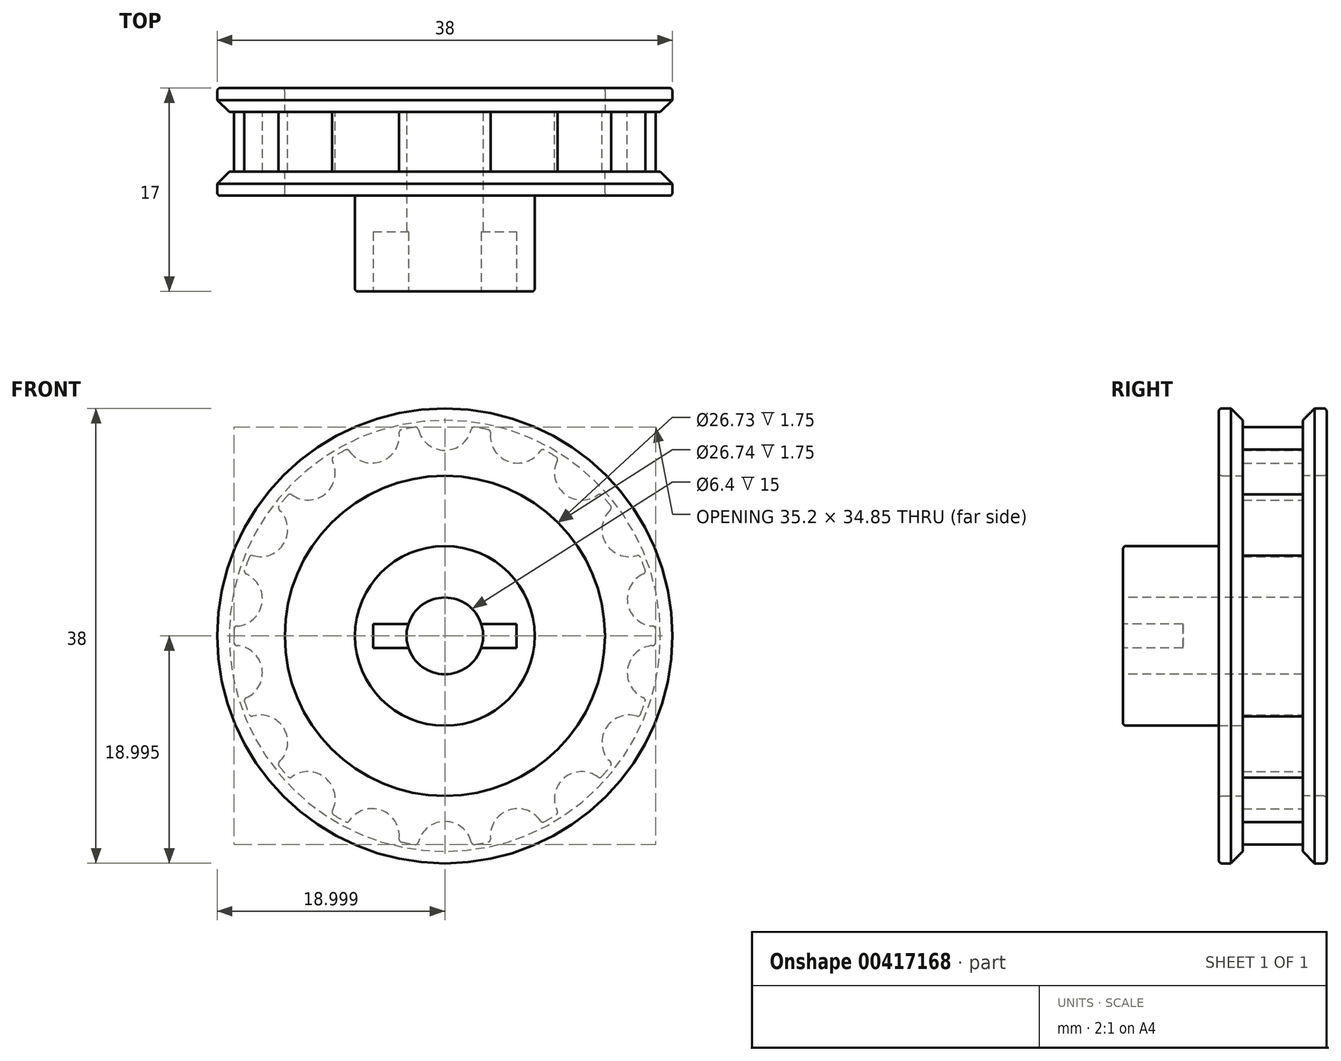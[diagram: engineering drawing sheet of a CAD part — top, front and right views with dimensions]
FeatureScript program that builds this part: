
annotation { "Feature Type Name" : "Feature", "Feature Type Description" : "" }
export const myFeature = defineFeature(function(context is Context, id is Id, definition is map)
    precondition{}
    {
        {
            var Q0;
            Q0=qCreatedBy(makeId("Front.planeOp"),FACE);
            var sketch = newSketch(context, id + "F0", { "sketchPlane" : qUnion([Q0])});
            skCircle(sketch, "E0", {"center": v(-33.37, 18.9) * mm, "radius": 20.2 * mm});
            skCircle(sketch, "E1", {"center": v(-33.37, 18.9) * mm, "radius": 17.78 * mm, "construction": true});
            skCircle(sketch, "E2", {"center": v(-33.37, 36.69) * mm, "radius": 2.28 * mm});
            skCircle(sketch, "E3.1.0", {"center": v(-39.45, 35.61) * mm, "radius": 2.28 * mm});
            skCircle(sketch, "E3.2.0", {"center": v(-44.8, 32.53) * mm, "radius": 2.28 * mm});
            skCircle(sketch, "E3.3.0", {"center": v(-48.77, 27.8) * mm, "radius": 2.28 * mm});
            skCircle(sketch, "E3.4.0", {"center": v(-50.88, 22) * mm, "radius": 2.28 * mm});
            skCircle(sketch, "E3.5.0", {"center": v(-50.88, 15.82) * mm, "radius": 2.28 * mm});
            skCircle(sketch, "E3.6.0", {"center": v(-48.77, 10.01) * mm, "radius": 2.28 * mm});
            skCircle(sketch, "E3.7.0", {"center": v(-44.8, 5.28) * mm, "radius": 2.28 * mm});
            skCircle(sketch, "E3.8.0", {"center": v(-39.45, 2.2) * mm, "radius": 2.28 * mm});
            skCircle(sketch, "E3.9.0", {"center": v(-33.37, 1.12) * mm, "radius": 2.28 * mm});
            skCircle(sketch, "E3.10.0", {"center": v(-27.29, 2.2) * mm, "radius": 2.28 * mm});
            skCircle(sketch, "E3.11.0", {"center": v(-21.94, 5.28) * mm, "radius": 2.28 * mm});
            skCircle(sketch, "E3.12.0", {"center": v(-17.97, 10.01) * mm, "radius": 2.28 * mm});
            skCircle(sketch, "E3.13.0", {"center": v(-15.86, 15.82) * mm, "radius": 2.28 * mm});
            skCircle(sketch, "E3.14.0", {"center": v(-15.86, 22) * mm, "radius": 2.28 * mm});
            skCircle(sketch, "E3.15.0", {"center": v(-17.97, 27.8) * mm, "radius": 2.28 * mm});
            skCircle(sketch, "E3.16.0", {"center": v(-21.94, 32.53) * mm, "radius": 2.28 * mm});
            skCircle(sketch, "E3.17.0", {"center": v(-27.29, 35.61) * mm, "radius": 2.28 * mm});
            skSolve(sketch);
        }
        {
            var Q0;
            Q0 = qSketchRegion(id + "F0", true);
            extrude(context, id + "F1", {"entities" : qUnion([Q0]), "depth" : 5 * mm, "offsetDistance" : 25 * mm});
        }
        {
            var Q0;
            Q0=makeQuery(id+"F1.opExtrude","CAP_FACE",FACE,{"disambiguationData":[OSD([sQuery(id+"F0.wireOp",EDGE,"E0"),sQuery(id+"F0.wireOp",EDGE,"E2"),sQuery(id+"F0.wireOp",EDGE,"E3.1.0"),sQuery(id+"F0.wireOp",EDGE,"E3.2.0"),sQuery(id+"F0.wireOp",EDGE,"E3.3.0"),sQuery(id+"F0.wireOp",EDGE,"E3.4.0"),sQuery(id+"F0.wireOp",EDGE,"E3.5.0"),sQuery(id+"F0.wireOp",EDGE,"E3.6.0"),sQuery(id+"F0.wireOp",EDGE,"E3.7.0"),sQuery(id+"F0.wireOp",EDGE,"E3.8.0"),sQuery(id+"F0.wireOp",EDGE,"E3.9.0"),sQuery(id+"F0.wireOp",EDGE,"E3.10.0"),sQuery(id+"F0.wireOp",EDGE,"E3.11.0"),sQuery(id+"F0.wireOp",EDGE,"E3.12.0"),sQuery(id+"F0.wireOp",EDGE,"E3.13.0"),sQuery(id+"F0.wireOp",EDGE,"E3.14.0"),sQuery(id+"F0.wireOp",EDGE,"E3.15.0"),sQuery(id+"F0.wireOp",EDGE,"E3.16.0"),sQuery(id+"F0.wireOp",EDGE,"E3.17.0"),sQuery(id+"F0.wireOp",EDGE,"E3.18.0"),sQuery(id+"F0.wireOp",EDGE,"E3.19.0")])],"isStart":false});
            var sketch = newSketch(context, id + "F2", { "sketchPlane" : qUnion([Q0])});
            skCircle(sketch, "E4", {"center": v(-33.37, 18.9) * mm, "radius": 17.6 * mm});
            skCircle(sketch, "E5", {"center": v(-33.37, 18.9) * mm, "radius": 21.36 * mm});
            skSolve(sketch);
        }
        {
            var Q0;
            Q0 = qSketchRegion(id + "F2", true);
            extrude(context, id + "F3", {"entities" : qUnion([Q0]), "operationType" : NewBodyOperationType.REMOVE, "oppositeDirection" : true, "depth" : 5 * mm, "offsetDistance" : 25 * mm});
        }
        {
            var Q0;
            Q0=makeQuery(id+"F1.opExtrude","CAP_FACE",FACE,{"disambiguationData":[OSD([sQuery(id+"F0.wireOp",EDGE,"E0"),sQuery(id+"F0.wireOp",EDGE,"E2"),sQuery(id+"F0.wireOp",EDGE,"E3.1.0"),sQuery(id+"F0.wireOp",EDGE,"E3.2.0"),sQuery(id+"F0.wireOp",EDGE,"E3.3.0"),sQuery(id+"F0.wireOp",EDGE,"E3.4.0"),sQuery(id+"F0.wireOp",EDGE,"E3.5.0"),sQuery(id+"F0.wireOp",EDGE,"E3.6.0"),sQuery(id+"F0.wireOp",EDGE,"E3.7.0"),sQuery(id+"F0.wireOp",EDGE,"E3.8.0"),sQuery(id+"F0.wireOp",EDGE,"E3.9.0"),sQuery(id+"F0.wireOp",EDGE,"E3.10.0"),sQuery(id+"F0.wireOp",EDGE,"E3.11.0"),sQuery(id+"F0.wireOp",EDGE,"E3.12.0"),sQuery(id+"F0.wireOp",EDGE,"E3.13.0"),sQuery(id+"F0.wireOp",EDGE,"E3.14.0"),sQuery(id+"F0.wireOp",EDGE,"E3.15.0"),sQuery(id+"F0.wireOp",EDGE,"E3.16.0"),sQuery(id+"F0.wireOp",EDGE,"E3.17.0"),sQuery(id+"F0.wireOp",EDGE,"E3.18.0"),sQuery(id+"F0.wireOp",EDGE,"E3.19.0")])],"isStart":false});
            var sketch = newSketch(context, id + "F4", { "sketchPlane" : qUnion([Q0])});
            skCircle(sketch, "E6", {"center": v(-33.37, 18.9) * mm, "radius": 13.37 * mm});
            skCircle(sketch, "E7", {"center": v(-33.37, 18.9) * mm, "radius": 19 * mm});
            skSolve(sketch);
        }
        {
            var Q0;
            Q0=makeQuery(id+"F4.imprint","IMPRINT",FACE,{"disambiguationData":[TD([[makeQuery(id+"F4.imprint","IMPRINT",EDGE,{"derivedFrom":sQuery(id+"F4.wireOp",EDGE,"E7")}),1.0]])]});
            var Q1;
            Q1=makeQuery(id+"F4.imprint","IMPRINT",FACE,{"disambiguationData":[TD([[makeQuery(id+"F4.imprint","IMPRINT",EDGE,{"derivedFrom":sQuery(id+"F4.wireOp",EDGE,"E6")}),-1.0]])]});
            extrude(context, id + "F5", {"entities" : qUnion([Q0, Q1]), "operationType" : NewBodyOperationType.ADD, "depth" : 2 * mm, "offsetDistance" : 25 * mm});
        }
        {
            var Q0;
            Q0=makeQuery(id+"F5.opExtrude","CAP_EDGE",EDGE,{"disambiguationData":[OSD([sQuery(id+"F4.wireOp",EDGE,"E7")])],"isStart":true});
            chamfer(context, id + "F6", {"entities" : qUnion([Q0]), "chamferType" : ChamferType.OFFSET_ANGLE, "width" : 1 * mm, "oppositeDirection" : false, "angle" : 45 * degree, "tangentPropagation" : true});
        }
        {
            var Q0;
            Q0=makeQuery(id+"F1.opExtrude","CAP_FACE",FACE,{"disambiguationData":[OSD([sQuery(id+"F0.wireOp",EDGE,"E0"),sQuery(id+"F0.wireOp",EDGE,"E2"),sQuery(id+"F0.wireOp",EDGE,"E3.1.0"),sQuery(id+"F0.wireOp",EDGE,"E3.2.0"),sQuery(id+"F0.wireOp",EDGE,"E3.3.0"),sQuery(id+"F0.wireOp",EDGE,"E3.4.0"),sQuery(id+"F0.wireOp",EDGE,"E3.5.0"),sQuery(id+"F0.wireOp",EDGE,"E3.6.0"),sQuery(id+"F0.wireOp",EDGE,"E3.7.0"),sQuery(id+"F0.wireOp",EDGE,"E3.8.0"),sQuery(id+"F0.wireOp",EDGE,"E3.9.0"),sQuery(id+"F0.wireOp",EDGE,"E3.10.0"),sQuery(id+"F0.wireOp",EDGE,"E3.11.0"),sQuery(id+"F0.wireOp",EDGE,"E3.12.0"),sQuery(id+"F0.wireOp",EDGE,"E3.13.0"),sQuery(id+"F0.wireOp",EDGE,"E3.14.0"),sQuery(id+"F0.wireOp",EDGE,"E3.15.0"),sQuery(id+"F0.wireOp",EDGE,"E3.16.0"),sQuery(id+"F0.wireOp",EDGE,"E3.17.0"),sQuery(id+"F0.wireOp",EDGE,"E3.18.0"),sQuery(id+"F0.wireOp",EDGE,"E3.19.0")])],"isStart":true});
            var sketch = newSketch(context, id + "F7", { "sketchPlane" : qUnion([Q0])});
            skCircle(sketch, "E8", {"center": v(33.37, 18.9) * mm, "radius": 13.37 * mm});
            skCircle(sketch, "E9", {"center": v(33.37, 18.9) * mm, "radius": 19 * mm});
            skSolve(sketch);
        }
        {
            var Q0;
            Q0=makeQuery(id+"F7.imprint","IMPRINT",FACE,{"disambiguationData":[TD([[makeQuery(id+"F7.imprint","IMPRINT",EDGE,{"derivedFrom":sQuery(id+"F7.wireOp",EDGE,"E8")}),-1.0]])]});
            var Q1;
            Q1=makeQuery(id+"F7.imprint","IMPRINT",FACE,{"disambiguationData":[TD([[makeQuery(id+"F7.imprint","IMPRINT",EDGE,{"derivedFrom":sQuery(id+"F7.wireOp",EDGE,"E9")}),1.0]])]});
            extrude(context, id + "F8", {"entities" : qUnion([Q0, Q1]), "operationType" : NewBodyOperationType.ADD, "depth" : 2 * mm, "offsetDistance" : 25 * mm});
        }
        {
            var Q0;
            Q0=makeQuery(id+"F8.opExtrude","CAP_EDGE",EDGE,{"disambiguationData":[OSD([sQuery(id+"F7.wireOp",EDGE,"E9")])],"isStart":true});
            chamfer(context, id + "F9", {"entities" : qUnion([Q0]), "chamferType" : ChamferType.OFFSET_ANGLE, "width" : 1 * mm, "oppositeDirection" : false, "angle" : 45 * degree, "tangentPropagation" : true});
        }
        {
            var Q0;
            Q0=makeQuery(id+"F1.opExtrude","CAP_FACE",FACE,{"disambiguationData":[OSD([sQuery(id+"F0.wireOp",EDGE,"E0"),sQuery(id+"F0.wireOp",EDGE,"E2"),sQuery(id+"F0.wireOp",EDGE,"E3.1.0"),sQuery(id+"F0.wireOp",EDGE,"E3.2.0"),sQuery(id+"F0.wireOp",EDGE,"E3.3.0"),sQuery(id+"F0.wireOp",EDGE,"E3.4.0"),sQuery(id+"F0.wireOp",EDGE,"E3.5.0"),sQuery(id+"F0.wireOp",EDGE,"E3.6.0"),sQuery(id+"F0.wireOp",EDGE,"E3.7.0"),sQuery(id+"F0.wireOp",EDGE,"E3.8.0"),sQuery(id+"F0.wireOp",EDGE,"E3.9.0"),sQuery(id+"F0.wireOp",EDGE,"E3.10.0"),sQuery(id+"F0.wireOp",EDGE,"E3.11.0"),sQuery(id+"F0.wireOp",EDGE,"E3.12.0"),sQuery(id+"F0.wireOp",EDGE,"E3.13.0"),sQuery(id+"F0.wireOp",EDGE,"E3.14.0"),sQuery(id+"F0.wireOp",EDGE,"E3.15.0"),sQuery(id+"F0.wireOp",EDGE,"E3.16.0"),sQuery(id+"F0.wireOp",EDGE,"E3.17.0"),sQuery(id+"F0.wireOp",EDGE,"E3.18.0"),sQuery(id+"F0.wireOp",EDGE,"E3.19.0")])],"isStart":false});
            var sketch = newSketch(context, id + "F10", { "sketchPlane" : qUnion([Q0])});
            skCircle(sketch, "E10", {"center": v(-33.37, 18.9) * mm, "radius": 7.5 * mm});
            skSolve(sketch);
        }
        {
            var Q0;
            Q0=makeQuery(id+"F10.imprint","IMPRINT",FACE,{"disambiguationData":[TD([[makeQuery(id+"F10.imprint","IMPRINT",EDGE,{"derivedFrom":sQuery(id+"F10.wireOp",EDGE,"E10")}),1.0]])]});
            extrude(context, id + "F11", {"entities" : qUnion([Q0]), "operationType" : NewBodyOperationType.ADD, "depth" : 10 * mm, "offsetDistance" : 25 * mm});
        }
        {
            var Q0;
            Q0=makeQuery(id+"F11.opExtrude","CAP_FACE",FACE,{"disambiguationData":[OSD([sQuery(id+"F10.wireOp",EDGE,"E10")])],"isStart":false});
            var sketch = newSketch(context, id + "F12", { "sketchPlane" : qUnion([Q0])});
            skCircle(sketch, "E11", {"center": v(-33.37, 18.9) * mm, "radius": 3.2 * mm});
            skSolve(sketch);
        }
        {
            var Q0;
            Q0=makeQuery(id+"F12.imprint","IMPRINT",FACE,{"disambiguationData":[TD([[makeQuery(id+"F12.imprint","IMPRINT",EDGE,{"derivedFrom":sQuery(id+"F12.wireOp",EDGE,"E11")}),1.0]])]});
            extrude(context, id + "F13", {"entities" : qUnion([Q0]), "operationType" : NewBodyOperationType.REMOVE, "oppositeDirection" : true, "depth" : 15 * mm, "offsetDistance" : 25 * mm});
        }
        {
            var Q0;
            Q0=makeQuery(id+"F11.opExtrude","CAP_FACE",FACE,{"disambiguationData":[OSD([sQuery(id+"F10.wireOp",EDGE,"E10")])],"isStart":false});
            var sketch = newSketch(context, id + "F14", { "sketchPlane" : qUnion([Q0])});
            skLineSegment(sketch, "E12.bottom", {"start": v(-39.37, 19.9) * mm, "end": v(-27.37, 19.9) * mm});
            skLineSegment(sketch, "E12.top", {"start": v(-39.37, 17.9) * mm, "end": v(-27.37, 17.9) * mm});
            skLineSegment(sketch, "E12.left", {"start": v(-39.37, 19.9) * mm, "end": v(-39.37, 17.9) * mm});
            skLineSegment(sketch, "E12.right", {"start": v(-27.37, 19.9) * mm, "end": v(-27.37, 17.9) * mm});
            skPoint(sketch, "E12.middle", {"position": v(-33.37, 18.9) * mm});
            skSolve(sketch);
        }
        {
            var Q0;
            {var subQ0=sQuery(id+"F14.wireOp",EDGE,"E12.left");Q0=makeQuery(id+"F14.imprint","IMPRINT",FACE,{"disambiguationData":[TD([[makeQuery(id+"F14.imprint","IMPRINT",EDGE,{"derivedFrom":subQ0}),1.0]])]});}
            var Q1;
            {var subQ0=sQuery(id+"F14.wireOp",EDGE,"E12.right");Q1=makeQuery(id+"F14.imprint","IMPRINT",FACE,{"disambiguationData":[TD([[makeQuery(id+"F14.imprint","IMPRINT",EDGE,{"derivedFrom":subQ0}),-1.0]])]});}
            extrude(context, id + "F15", {"entities" : qUnion([Q0, Q1]), "operationType" : NewBodyOperationType.REMOVE, "oppositeDirection" : true, "depth" : 5 * mm, "offsetDistance" : 25 * mm});
        }
        {
            var Q0;
            Q0=makeQuery(id+"F3.boolean.opBoolean","INTERSECT",EDGE,{"disambiguationData":[OD(1.0)],"derivedFrom":[makeQuery(id+"F1.opExtrude","SWEPT_FACE",FACE,{"disambiguationData":[OSD([sQuery(id+"F0.wireOp",EDGE,"E3.11.0")])]}),makeQuery(id+"F3.opExtrude","SWEPT_FACE",FACE,{"disambiguationData":[OSD([sQuery(id+"F2.wireOp",EDGE,"E4")])]})]});
            var Q1;
            Q1=makeQuery(id+"F3.boolean.opBoolean","INTERSECT",EDGE,{"disambiguationData":[OD(0.0)],"derivedFrom":[makeQuery(id+"F1.opExtrude","SWEPT_FACE",FACE,{"disambiguationData":[OSD([sQuery(id+"F0.wireOp",EDGE,"E3.11.0")])]}),makeQuery(id+"F3.opExtrude","SWEPT_FACE",FACE,{"disambiguationData":[OSD([sQuery(id+"F2.wireOp",EDGE,"E4")])]})]});
            var Q2;
            Q2=makeQuery(id+"F3.boolean.opBoolean","INTERSECT",EDGE,{"disambiguationData":[OD(1.0)],"derivedFrom":[makeQuery(id+"F1.opExtrude","SWEPT_FACE",FACE,{"disambiguationData":[OSD([sQuery(id+"F0.wireOp",EDGE,"E3.10.0")])]}),makeQuery(id+"F3.opExtrude","SWEPT_FACE",FACE,{"disambiguationData":[OSD([sQuery(id+"F2.wireOp",EDGE,"E4")])]})]});
            var Q3;
            Q3=makeQuery(id+"F3.boolean.opBoolean","INTERSECT",EDGE,{"disambiguationData":[OD(0.0)],"derivedFrom":[makeQuery(id+"F1.opExtrude","SWEPT_FACE",FACE,{"disambiguationData":[OSD([sQuery(id+"F0.wireOp",EDGE,"E3.12.0")])]}),makeQuery(id+"F3.opExtrude","SWEPT_FACE",FACE,{"disambiguationData":[OSD([sQuery(id+"F2.wireOp",EDGE,"E4")])]})]});
            var Q4;
            Q4=makeQuery(id+"F3.boolean.opBoolean","INTERSECT",EDGE,{"disambiguationData":[OD(1.0)],"derivedFrom":[makeQuery(id+"F1.opExtrude","SWEPT_FACE",FACE,{"disambiguationData":[OSD([sQuery(id+"F0.wireOp",EDGE,"E3.12.0")])]}),makeQuery(id+"F3.opExtrude","SWEPT_FACE",FACE,{"disambiguationData":[OSD([sQuery(id+"F2.wireOp",EDGE,"E4")])]})]});
            var Q5;
            Q5=makeQuery(id+"F3.boolean.opBoolean","INTERSECT",EDGE,{"disambiguationData":[OD(0.0)],"derivedFrom":[makeQuery(id+"F1.opExtrude","SWEPT_FACE",FACE,{"disambiguationData":[OSD([sQuery(id+"F0.wireOp",EDGE,"E3.13.0")])]}),makeQuery(id+"F3.opExtrude","SWEPT_FACE",FACE,{"disambiguationData":[OSD([sQuery(id+"F2.wireOp",EDGE,"E4")])]})]});
            var Q6;
            Q6=makeQuery(id+"F3.boolean.opBoolean","INTERSECT",EDGE,{"disambiguationData":[OD(1.0)],"derivedFrom":[makeQuery(id+"F1.opExtrude","SWEPT_FACE",FACE,{"disambiguationData":[OSD([sQuery(id+"F0.wireOp",EDGE,"E3.13.0")])]}),makeQuery(id+"F3.opExtrude","SWEPT_FACE",FACE,{"disambiguationData":[OSD([sQuery(id+"F2.wireOp",EDGE,"E4")])]})]});
            var Q7;
            Q7=makeQuery(id+"F3.boolean.opBoolean","INTERSECT",EDGE,{"disambiguationData":[OD(0.0)],"derivedFrom":[makeQuery(id+"F1.opExtrude","SWEPT_FACE",FACE,{"disambiguationData":[OSD([sQuery(id+"F0.wireOp",EDGE,"E3.14.0")])]}),makeQuery(id+"F3.opExtrude","SWEPT_FACE",FACE,{"disambiguationData":[OSD([sQuery(id+"F2.wireOp",EDGE,"E4")])]})]});
            var Q8;
            Q8=makeQuery(id+"F3.boolean.opBoolean","INTERSECT",EDGE,{"disambiguationData":[OD(1.0)],"derivedFrom":[makeQuery(id+"F1.opExtrude","SWEPT_FACE",FACE,{"disambiguationData":[OSD([sQuery(id+"F0.wireOp",EDGE,"E3.14.0")])]}),makeQuery(id+"F3.opExtrude","SWEPT_FACE",FACE,{"disambiguationData":[OSD([sQuery(id+"F2.wireOp",EDGE,"E4")])]})]});
            var Q9;
            Q9=makeQuery(id+"F3.boolean.opBoolean","INTERSECT",EDGE,{"disambiguationData":[OD(0.0)],"derivedFrom":[makeQuery(id+"F1.opExtrude","SWEPT_FACE",FACE,{"disambiguationData":[OSD([sQuery(id+"F0.wireOp",EDGE,"E3.15.0")])]}),makeQuery(id+"F3.opExtrude","SWEPT_FACE",FACE,{"disambiguationData":[OSD([sQuery(id+"F2.wireOp",EDGE,"E4")])]})]});
            fillet(context, id + "F16", {"entities" : qUnion([Q0, Q1, Q2, Q3, Q4, Q5, Q6, Q7, Q8, Q9]), "radius" : .25 * mm, "tangentPropagation" : true, "allowEdgeOverflow" : false});
        }
        {
            var Q0;
            Q0=makeQuery(id+"F3.boolean.opBoolean","INTERSECT",EDGE,{"disambiguationData":[OD(1.0)],"derivedFrom":[makeQuery(id+"F1.opExtrude","SWEPT_FACE",FACE,{"disambiguationData":[OSD([sQuery(id+"F0.wireOp",EDGE,"E3.15.0")])]}),makeQuery(id+"F3.opExtrude","SWEPT_FACE",FACE,{"disambiguationData":[OSD([sQuery(id+"F2.wireOp",EDGE,"E4")])]})]});
            var Q1;
            Q1=makeQuery(id+"F3.boolean.opBoolean","INTERSECT",EDGE,{"disambiguationData":[OD(0.0)],"derivedFrom":[makeQuery(id+"F1.opExtrude","SWEPT_FACE",FACE,{"disambiguationData":[OSD([sQuery(id+"F0.wireOp",EDGE,"E3.16.0")])]}),makeQuery(id+"F3.opExtrude","SWEPT_FACE",FACE,{"disambiguationData":[OSD([sQuery(id+"F2.wireOp",EDGE,"E4")])]})]});
            var Q2;
            Q2=makeQuery(id+"F3.boolean.opBoolean","INTERSECT",EDGE,{"disambiguationData":[OD(1.0)],"derivedFrom":[makeQuery(id+"F1.opExtrude","SWEPT_FACE",FACE,{"disambiguationData":[OSD([sQuery(id+"F0.wireOp",EDGE,"E3.16.0")])]}),makeQuery(id+"F3.opExtrude","SWEPT_FACE",FACE,{"disambiguationData":[OSD([sQuery(id+"F2.wireOp",EDGE,"E4")])]})]});
            var Q3;
            Q3=makeQuery(id+"F3.boolean.opBoolean","INTERSECT",EDGE,{"disambiguationData":[OD(1.0)],"derivedFrom":[makeQuery(id+"F1.opExtrude","SWEPT_FACE",FACE,{"disambiguationData":[OSD([sQuery(id+"F0.wireOp",EDGE,"E3.17.0")])]}),makeQuery(id+"F3.opExtrude","SWEPT_FACE",FACE,{"disambiguationData":[OSD([sQuery(id+"F2.wireOp",EDGE,"E4")])]})]});
            var Q4;
            Q4=makeQuery(id+"F3.boolean.opBoolean","INTERSECT",EDGE,{"disambiguationData":[OD(0.0)],"derivedFrom":[makeQuery(id+"F1.opExtrude","SWEPT_FACE",FACE,{"disambiguationData":[OSD([sQuery(id+"F0.wireOp",EDGE,"E3.17.0")])]}),makeQuery(id+"F3.opExtrude","SWEPT_FACE",FACE,{"disambiguationData":[OSD([sQuery(id+"F2.wireOp",EDGE,"E4")])]})]});
            var Q5;
            Q5=makeQuery(id+"F3.boolean.opBoolean","INTERSECT",EDGE,{"disambiguationData":[OD(1.0)],"derivedFrom":[makeQuery(id+"F1.opExtrude","SWEPT_FACE",FACE,{"disambiguationData":[OSD([sQuery(id+"F0.wireOp",EDGE,"E2")])]}),makeQuery(id+"F3.opExtrude","SWEPT_FACE",FACE,{"disambiguationData":[OSD([sQuery(id+"F2.wireOp",EDGE,"E4")])]})]});
            var Q6;
            Q6=makeQuery(id+"F3.boolean.opBoolean","INTERSECT",EDGE,{"disambiguationData":[OD(0.0)],"derivedFrom":[makeQuery(id+"F1.opExtrude","SWEPT_FACE",FACE,{"disambiguationData":[OSD([sQuery(id+"F0.wireOp",EDGE,"E2")])]}),makeQuery(id+"F3.opExtrude","SWEPT_FACE",FACE,{"disambiguationData":[OSD([sQuery(id+"F2.wireOp",EDGE,"E4")])]})]});
            var Q7;
            Q7=makeQuery(id+"F3.boolean.opBoolean","INTERSECT",EDGE,{"disambiguationData":[OD(0.0)],"derivedFrom":[makeQuery(id+"F1.opExtrude","SWEPT_FACE",FACE,{"disambiguationData":[OSD([sQuery(id+"F0.wireOp",EDGE,"E3.1.0")])]}),makeQuery(id+"F3.opExtrude","SWEPT_FACE",FACE,{"disambiguationData":[OSD([sQuery(id+"F2.wireOp",EDGE,"E4")])]})]});
            var Q8;
            Q8=makeQuery(id+"F3.boolean.opBoolean","INTERSECT",EDGE,{"disambiguationData":[OD(1.0)],"derivedFrom":[makeQuery(id+"F1.opExtrude","SWEPT_FACE",FACE,{"disambiguationData":[OSD([sQuery(id+"F0.wireOp",EDGE,"E3.1.0")])]}),makeQuery(id+"F3.opExtrude","SWEPT_FACE",FACE,{"disambiguationData":[OSD([sQuery(id+"F2.wireOp",EDGE,"E4")])]})]});
            var Q9;
            Q9=makeQuery(id+"F3.boolean.opBoolean","INTERSECT",EDGE,{"disambiguationData":[OD(0.0)],"derivedFrom":[makeQuery(id+"F1.opExtrude","SWEPT_FACE",FACE,{"disambiguationData":[OSD([sQuery(id+"F0.wireOp",EDGE,"E3.2.0")])]}),makeQuery(id+"F3.opExtrude","SWEPT_FACE",FACE,{"disambiguationData":[OSD([sQuery(id+"F2.wireOp",EDGE,"E4")])]})]});
            var Q10;
            Q10=makeQuery(id+"F3.boolean.opBoolean","INTERSECT",EDGE,{"disambiguationData":[OD(1.0)],"derivedFrom":[makeQuery(id+"F1.opExtrude","SWEPT_FACE",FACE,{"disambiguationData":[OSD([sQuery(id+"F0.wireOp",EDGE,"E3.2.0")])]}),makeQuery(id+"F3.opExtrude","SWEPT_FACE",FACE,{"disambiguationData":[OSD([sQuery(id+"F2.wireOp",EDGE,"E4")])]})]});
            var Q11;
            Q11=makeQuery(id+"F3.boolean.opBoolean","INTERSECT",EDGE,{"disambiguationData":[OD(0.0)],"derivedFrom":[makeQuery(id+"F1.opExtrude","SWEPT_FACE",FACE,{"disambiguationData":[OSD([sQuery(id+"F0.wireOp",EDGE,"E3.3.0")])]}),makeQuery(id+"F3.opExtrude","SWEPT_FACE",FACE,{"disambiguationData":[OSD([sQuery(id+"F2.wireOp",EDGE,"E4")])]})]});
            var Q12;
            Q12=makeQuery(id+"F3.boolean.opBoolean","INTERSECT",EDGE,{"disambiguationData":[OD(1.0)],"derivedFrom":[makeQuery(id+"F1.opExtrude","SWEPT_FACE",FACE,{"disambiguationData":[OSD([sQuery(id+"F0.wireOp",EDGE,"E3.3.0")])]}),makeQuery(id+"F3.opExtrude","SWEPT_FACE",FACE,{"disambiguationData":[OSD([sQuery(id+"F2.wireOp",EDGE,"E4")])]})]});
            var Q13;
            Q13=makeQuery(id+"F3.boolean.opBoolean","INTERSECT",EDGE,{"disambiguationData":[OD(0.0)],"derivedFrom":[makeQuery(id+"F1.opExtrude","SWEPT_FACE",FACE,{"disambiguationData":[OSD([sQuery(id+"F0.wireOp",EDGE,"E3.4.0")])]}),makeQuery(id+"F3.opExtrude","SWEPT_FACE",FACE,{"disambiguationData":[OSD([sQuery(id+"F2.wireOp",EDGE,"E4")])]})]});
            var Q14;
            Q14=makeQuery(id+"F3.boolean.opBoolean","INTERSECT",EDGE,{"disambiguationData":[OD(1.0)],"derivedFrom":[makeQuery(id+"F1.opExtrude","SWEPT_FACE",FACE,{"disambiguationData":[OSD([sQuery(id+"F0.wireOp",EDGE,"E3.4.0")])]}),makeQuery(id+"F3.opExtrude","SWEPT_FACE",FACE,{"disambiguationData":[OSD([sQuery(id+"F2.wireOp",EDGE,"E4")])]})]});
            var Q15;
            Q15=makeQuery(id+"F3.boolean.opBoolean","INTERSECT",EDGE,{"disambiguationData":[OD(0.0)],"derivedFrom":[makeQuery(id+"F1.opExtrude","SWEPT_FACE",FACE,{"disambiguationData":[OSD([sQuery(id+"F0.wireOp",EDGE,"E3.5.0")])]}),makeQuery(id+"F3.opExtrude","SWEPT_FACE",FACE,{"disambiguationData":[OSD([sQuery(id+"F2.wireOp",EDGE,"E4")])]})]});
            var Q16;
            Q16=makeQuery(id+"F3.boolean.opBoolean","INTERSECT",EDGE,{"disambiguationData":[OD(1.0)],"derivedFrom":[makeQuery(id+"F1.opExtrude","SWEPT_FACE",FACE,{"disambiguationData":[OSD([sQuery(id+"F0.wireOp",EDGE,"E3.5.0")])]}),makeQuery(id+"F3.opExtrude","SWEPT_FACE",FACE,{"disambiguationData":[OSD([sQuery(id+"F2.wireOp",EDGE,"E4")])]})]});
            var Q17;
            Q17=makeQuery(id+"F3.boolean.opBoolean","INTERSECT",EDGE,{"disambiguationData":[OD(1.0)],"derivedFrom":[makeQuery(id+"F1.opExtrude","SWEPT_FACE",FACE,{"disambiguationData":[OSD([sQuery(id+"F0.wireOp",EDGE,"E3.6.0")])]}),makeQuery(id+"F3.opExtrude","SWEPT_FACE",FACE,{"disambiguationData":[OSD([sQuery(id+"F2.wireOp",EDGE,"E4")])]})]});
            var Q18;
            Q18=makeQuery(id+"F3.boolean.opBoolean","INTERSECT",EDGE,{"disambiguationData":[OD(0.0)],"derivedFrom":[makeQuery(id+"F1.opExtrude","SWEPT_FACE",FACE,{"disambiguationData":[OSD([sQuery(id+"F0.wireOp",EDGE,"E3.6.0")])]}),makeQuery(id+"F3.opExtrude","SWEPT_FACE",FACE,{"disambiguationData":[OSD([sQuery(id+"F2.wireOp",EDGE,"E4")])]})]});
            var Q19;
            Q19=makeQuery(id+"F3.boolean.opBoolean","INTERSECT",EDGE,{"disambiguationData":[OD(0.0)],"derivedFrom":[makeQuery(id+"F1.opExtrude","SWEPT_FACE",FACE,{"disambiguationData":[OSD([sQuery(id+"F0.wireOp",EDGE,"E3.7.0")])]}),makeQuery(id+"F3.opExtrude","SWEPT_FACE",FACE,{"disambiguationData":[OSD([sQuery(id+"F2.wireOp",EDGE,"E4")])]})]});
            fillet(context, id + "F17", {"entities" : qUnion([Q0, Q1, Q2, Q3, Q4, Q5, Q6, Q7, Q8, Q9, Q10, Q11, Q12, Q13, Q14, Q15, Q16, Q17, Q18, Q19]), "radius" : .25 * mm, "tangentPropagation" : true, "allowEdgeOverflow" : false});
        }
        {
            var Q0;
            Q0=makeQuery(id+"F3.boolean.opBoolean","INTERSECT",EDGE,{"disambiguationData":[OD(1.0)],"derivedFrom":[makeQuery(id+"F1.opExtrude","SWEPT_FACE",FACE,{"disambiguationData":[OSD([sQuery(id+"F0.wireOp",EDGE,"E3.7.0")])]}),makeQuery(id+"F3.opExtrude","SWEPT_FACE",FACE,{"disambiguationData":[OSD([sQuery(id+"F2.wireOp",EDGE,"E4")])]})]});
            var Q1;
            Q1=makeQuery(id+"F3.boolean.opBoolean","INTERSECT",EDGE,{"disambiguationData":[OD(0.0)],"derivedFrom":[makeQuery(id+"F1.opExtrude","SWEPT_FACE",FACE,{"disambiguationData":[OSD([sQuery(id+"F0.wireOp",EDGE,"E3.8.0")])]}),makeQuery(id+"F3.opExtrude","SWEPT_FACE",FACE,{"disambiguationData":[OSD([sQuery(id+"F2.wireOp",EDGE,"E4")])]})]});
            var Q2;
            Q2=makeQuery(id+"F3.boolean.opBoolean","INTERSECT",EDGE,{"disambiguationData":[OD(1.0)],"derivedFrom":[makeQuery(id+"F1.opExtrude","SWEPT_FACE",FACE,{"disambiguationData":[OSD([sQuery(id+"F0.wireOp",EDGE,"E3.8.0")])]}),makeQuery(id+"F3.opExtrude","SWEPT_FACE",FACE,{"disambiguationData":[OSD([sQuery(id+"F2.wireOp",EDGE,"E4")])]})]});
            var Q3;
            Q3=makeQuery(id+"F3.boolean.opBoolean","INTERSECT",EDGE,{"disambiguationData":[OD(0.0)],"derivedFrom":[makeQuery(id+"F1.opExtrude","SWEPT_FACE",FACE,{"disambiguationData":[OSD([sQuery(id+"F0.wireOp",EDGE,"E3.9.0")])]}),makeQuery(id+"F3.opExtrude","SWEPT_FACE",FACE,{"disambiguationData":[OSD([sQuery(id+"F2.wireOp",EDGE,"E4")])]})]});
            var Q4;
            Q4=makeQuery(id+"F3.boolean.opBoolean","INTERSECT",EDGE,{"disambiguationData":[OD(1.0)],"derivedFrom":[makeQuery(id+"F1.opExtrude","SWEPT_FACE",FACE,{"disambiguationData":[OSD([sQuery(id+"F0.wireOp",EDGE,"E3.9.0")])]}),makeQuery(id+"F3.opExtrude","SWEPT_FACE",FACE,{"disambiguationData":[OSD([sQuery(id+"F2.wireOp",EDGE,"E4")])]})]});
            var Q5;
            Q5=makeQuery(id+"F3.boolean.opBoolean","INTERSECT",EDGE,{"disambiguationData":[OD(0.0)],"derivedFrom":[makeQuery(id+"F1.opExtrude","SWEPT_FACE",FACE,{"disambiguationData":[OSD([sQuery(id+"F0.wireOp",EDGE,"E3.10.0")])]}),makeQuery(id+"F3.opExtrude","SWEPT_FACE",FACE,{"disambiguationData":[OSD([sQuery(id+"F2.wireOp",EDGE,"E4")])]})]});
            var Q6;
            Q6=makeQuery(id+"F5.opExtrude","CAP_EDGE",EDGE,{"disambiguationData":[OSD([sQuery(id+"F4.wireOp",EDGE,"E7")])],"isStart":false});
            var Q7;
            Q7=makeQuery(id+"F8.opExtrude","CAP_EDGE",EDGE,{"disambiguationData":[OSD([sQuery(id+"F7.wireOp",EDGE,"E9")])],"isStart":false});
            var Q8;
            Q8=makeQuery(id+"F11.opExtrude","CAP_EDGE",EDGE,{"disambiguationData":[OSD([sQuery(id+"F10.wireOp",EDGE,"E10")])],"isStart":false});
            var Q9;
            Q9=makeQuery(id+"F8.opExtrude","CAP_EDGE",EDGE,{"disambiguationData":[OSD([sQuery(id+"F7.wireOp",EDGE,"E8")])],"isStart":false});
            var Q10;
            Q10=makeQuery(id+"F8.opExtrude","CAP_EDGE",EDGE,{"disambiguationData":[OSD([sQuery(id+"F7.wireOp",EDGE,"E8")])],"isStart":true});
            fillet(context, id + "F18", {"entities" : qUnion([Q0, Q1, Q2, Q3, Q4, Q5, Q6, Q7, Q8, Q9, Q10]), "radius" : .25 * mm, "tangentPropagation" : true, "allowEdgeOverflow" : false});
        }
        {
            var Q0;
            Q0=makeQuery(id+"F5.opExtrude","CAP_EDGE",EDGE,{"disambiguationData":[OSD([sQuery(id+"F4.wireOp",EDGE,"E6")])],"isStart":false});
            var Q1;
            Q1=makeQuery(id+"F5.opExtrude","CAP_EDGE",EDGE,{"disambiguationData":[OSD([sQuery(id+"F4.wireOp",EDGE,"E6")])],"isStart":true});
            var Q2;
            Q2=makeQuery(id+"F11.opExtrude","CAP_EDGE",EDGE,{"disambiguationData":[OSD([sQuery(id+"F10.wireOp",EDGE,"E10")])],"isStart":true});
            fillet(context, id + "F19", {"entities" : qUnion([Q0, Q1, Q2]), "radius" : .25 * mm, "tangentPropagation" : true, "allowEdgeOverflow" : false});
        }
    });
